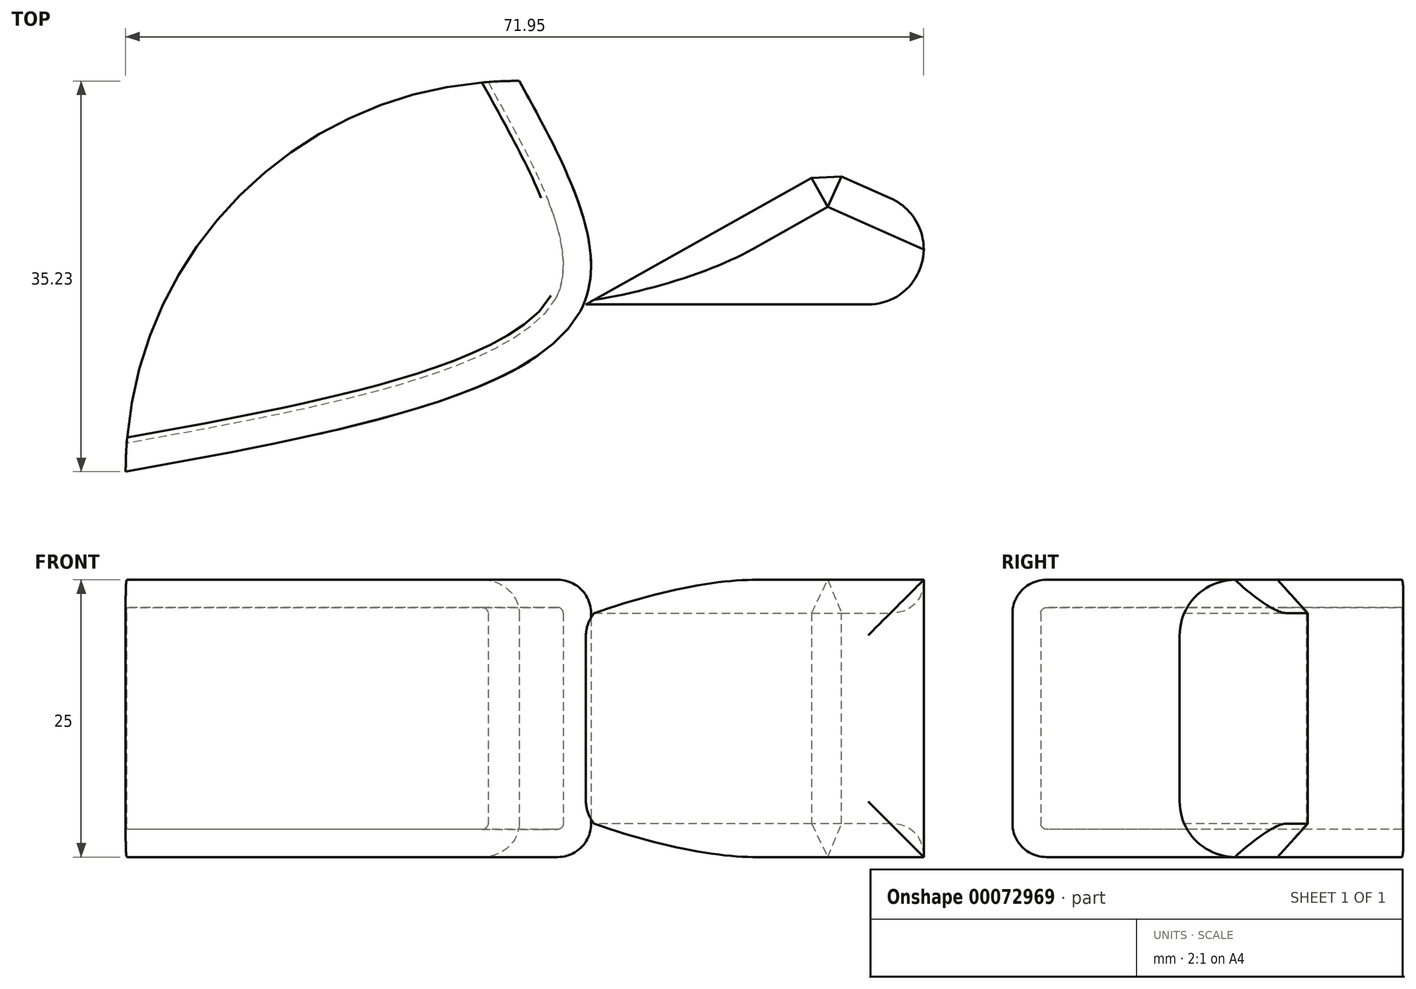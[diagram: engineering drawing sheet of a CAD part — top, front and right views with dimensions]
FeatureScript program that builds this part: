
annotation { "Feature Type Name" : "Feature", "Feature Type Description" : "" }
export const myFeature = defineFeature(function(context is Context, id is Id, definition is map)
    precondition{}
    {
        {
            var Q0;
            Q0=qCreatedBy(makeId("Top.planeOp"),FACE);
            var sketch = newSketch(context, id + "F0", { "sketchPlane" : qUnion([Q0])});
            skArc(sketch, "E0", {"start": v(0, 35.23) * mm, "mid": v(-25.08, 25) * mm, "end": v(-35.48, 0) * mm});
            skPoint(sketch, "E1", {"position": v(5.52, 14.49) * mm});
            skLineSegment(sketch, "E2", {"start": v(-22.93, 26.98) * mm, "end": v(5.52, 14.49) * mm});
            skFitSpline(sketch, "E3", {"points": [v(0, 35.23) * mm, v(5.52, 14.49) * mm, v(-35.48, 0) * mm], "startDerivative": vector(30.55, -55.56) * mm, "endDerivative": vector(-94.24, -17.14) * mm});
            skLineSegment(sketch, "E4.1.0.0", {"start": v(2.07, 26.98) * mm, "end": v(30.52, 14.49) * mm});
            skLineSegment(sketch, "E4.2.0.0", {"start": v(27.07, 26.98) * mm, "end": v(55.52, 14.49) * mm});
            skLineSegment(sketch, "E4.direction1", {"start": v(-22.93, 26.98) * mm, "end": v(2.07, 26.98) * mm, "construction": true});
            skSolve(sketch);
        }
        {
            var Q0;
            Q0=qCreatedBy(makeId("Top.planeOp"),FACE);
            var sketch = newSketch(context, id + "F1", { "sketchPlane" : qUnion([Q0])});
            skLineSegment(sketch, "E5", {"start": v(-22.86, 27.23) * mm, "end": v(27.68, 27.23) * mm});
            skLineSegment(sketch, "E6", {"start": v(27.68, 27.23) * mm, "end": v(6.02, 15.07) * mm});
            skLineSegment(sketch, "E7", {"start": v(6.02, 15.07) * mm, "end": v(55.03, 15.07) * mm});
            skLineSegment(sketch, "E8", {"start": v(55.03, 15.07) * mm, "end": v(27.68, 27.23) * mm});
            skSolve(sketch);
        }
        {
            var Q0;
            Q0 = qSketchRegion(id + "F0", true);
            extrude(context, id + "F2", {"entities" : qUnion([Q0]), "depth" : 25 * mm});
        }
        {
            var Q0;
            Q0 = qSketchRegion(id + "F1", true);
            extrude(context, id + "F3", {"entities" : qUnion([Q0]), "depth" : 25 * mm});
        }
        {
            var Q0;
            Q0=makeQuery(id+"F2.opExtrude","CAP_EDGE",EDGE,{"disambiguationData":[OSD([sQuery(id+"F0.wireOp",EDGE,"E3")])],"isStart":true});
            var Q1;
            Q1=makeQuery(id+"F2.opExtrude","CAP_EDGE",EDGE,{"disambiguationData":[OSD([sQuery(id+"F0.wireOp",EDGE,"E3")])],"isStart":false});
            fillet(context, id + "F4", {"entities" : qUnion([Q0, Q1]), "radius" : 3 * mm, "tangentPropagation" : true, "allowEdgeOverflow" : false});
        }
        {
            var Q0;
            Q0=makeQuery(id+"F3.opExtrude","CAP_EDGE",EDGE,{"disambiguationData":[OSD([sQuery(id+"F1.wireOp",EDGE,"E8")])],"isStart":false});
            var Q1;
            Q1=makeQuery(id+"F3.opExtrude","CAP_EDGE",EDGE,{"disambiguationData":[OSD([sQuery(id+"F1.wireOp",EDGE,"E8")])],"isStart":true});
            var Q2;
            Q2=makeQuery(id+"F3.opExtrude","SWEPT_EDGE",EDGE,{"disambiguationData":[OSD([sQuery(id+"F1.wireOp",EDGE,"E6"),sQuery(id+"F1.wireOp",EDGE,"E8")])]});
            var Q3;
            Q3=makeQuery(id+"F3.opExtrude","CAP_EDGE",EDGE,{"disambiguationData":[OSD([sQuery(id+"F1.wireOp",EDGE,"E6")])],"isStart":true});
            var Q4;
            Q4=makeQuery(id+"F3.opExtrude","CAP_EDGE",EDGE,{"disambiguationData":[OSD([sQuery(id+"F1.wireOp",EDGE,"E6")])],"isStart":false});
            chamfer(context, id + "F5", {"entities" : qUnion([Q0, Q1, Q2, Q3, Q4]), "width" : 3 * mm, "tangentPropagation" : true});
        }
        {
            var Q0;
            Q0=makeQuery(id+"F2.opExtrude","SWEPT_FACE",FACE,{"disambiguationData":[OSD([sQuery(id+"F0.wireOp",EDGE,"E0")])]});
            shell(context, id + "F6", {"entities" : qUnion([Q0]), "thickness" : 2.5 * mm});
        }
        {
            var Q0;
            Q0=makeQuery(id+"F3.opExtrude","SWEPT_EDGE",EDGE,{"disambiguationData":[OSD([sQuery(id+"F1.wireOp",EDGE,"E7"),sQuery(id+"F1.wireOp",EDGE,"E8")])]});
            var Q1;
            Q1=makeQuery(id+"F3.opExtrude","CAP_EDGE",EDGE,{"disambiguationData":[OSD([sQuery(id+"F1.wireOp",EDGE,"E7")])],"isStart":true});
            var Q2;
            Q2=makeQuery(id+"F3.opExtrude","CAP_EDGE",EDGE,{"disambiguationData":[OSD([sQuery(id+"F1.wireOp",EDGE,"E7")])],"isStart":false});
            fillet(context, id + "F7", {"entities" : qUnion([Q0, Q1, Q2]), "radius" : 5 * mm, "tangentPropagation" : true, "allowEdgeOverflow" : false});
        }
    });
